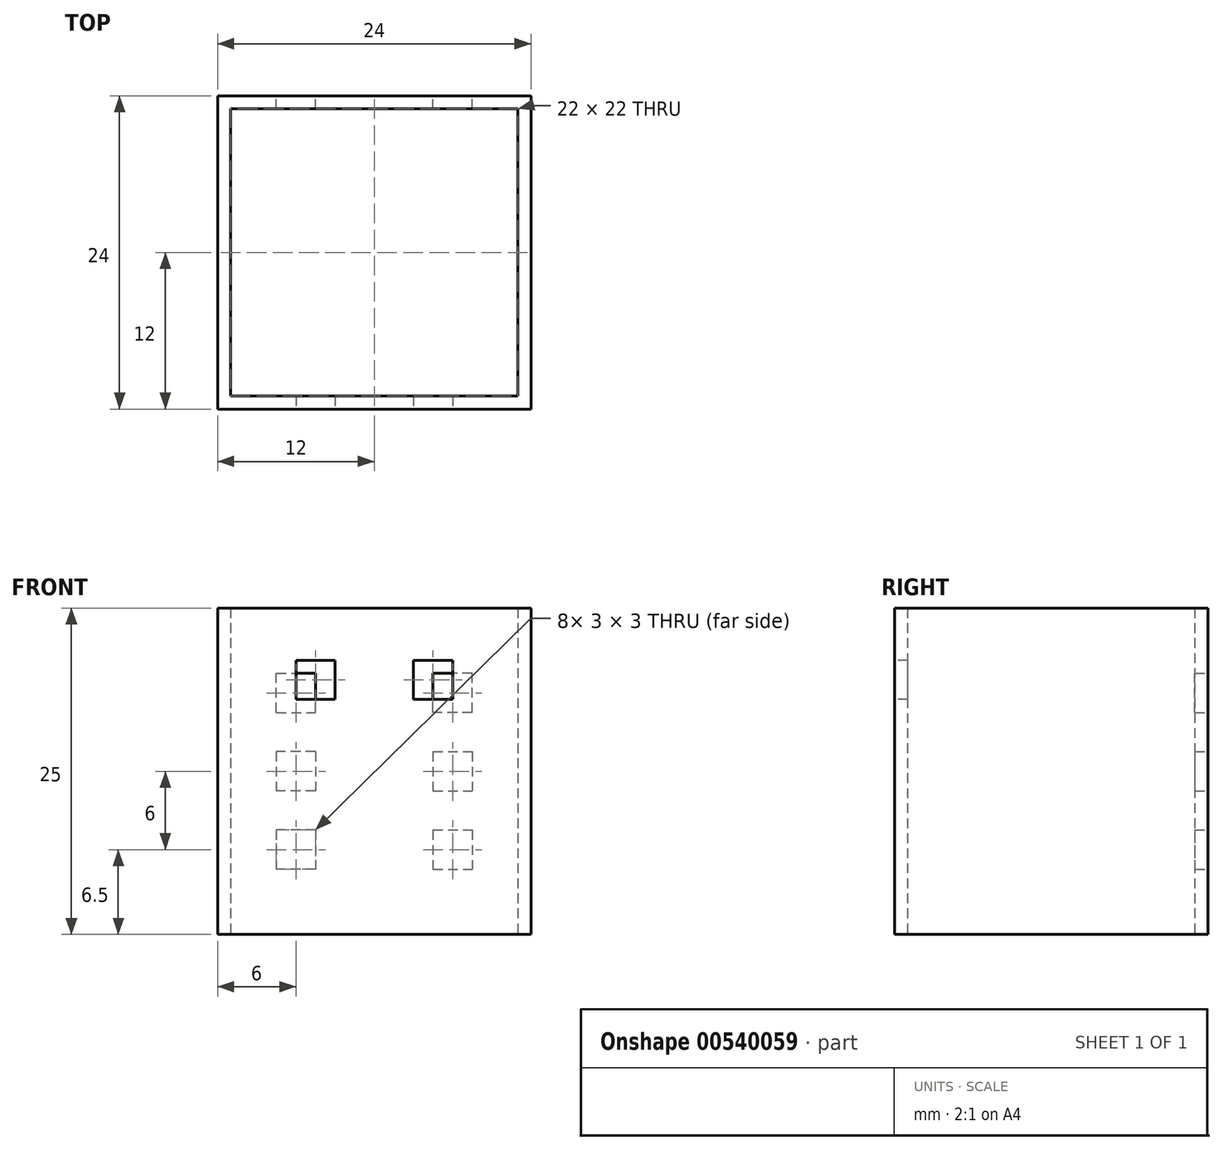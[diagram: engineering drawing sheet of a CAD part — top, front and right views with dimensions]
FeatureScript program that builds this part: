
annotation { "Feature Type Name" : "Feature", "Feature Type Description" : "" }
export const myFeature = defineFeature(function(context is Context, id is Id, definition is map)
    precondition{}
    {
        {
            var Q0;
            Q0=qCreatedBy(makeId("Top.planeOp"),FACE);
            var sketch = newSketch(context, id + "F0", { "sketchPlane" : qUnion([Q0])});
            skLineSegment(sketch, "E0.bottom", {"start": v(12, -12) * mm, "end": v(-12, -12) * mm});
            skLineSegment(sketch, "E0.top", {"start": v(12, 12) * mm, "end": v(-12, 12) * mm});
            skLineSegment(sketch, "E0.left", {"start": v(12, -12) * mm, "end": v(12, 12) * mm});
            skLineSegment(sketch, "E0.right", {"start": v(-12, -12) * mm, "end": v(-12, 12) * mm});
            skPoint(sketch, "E0.middle", {"position": v(0, 0) * mm});
            skLineSegment(sketch, "E1.bottom", {"start": v(11, -11) * mm, "end": v(-11, -11) * mm});
            skLineSegment(sketch, "E1.top", {"start": v(11, 11) * mm, "end": v(-11, 11) * mm});
            skLineSegment(sketch, "E1.left", {"start": v(11, -11) * mm, "end": v(11, 11) * mm});
            skLineSegment(sketch, "E1.right", {"start": v(-11, -11) * mm, "end": v(-11, 11) * mm});
            skSolve(sketch);
        }
        {
            var Q0;
            Q0=makeQuery(id+"F0.imprint","IMPRINT",FACE,{"disambiguationData":[TD([[makeQuery(id+"F0.imprint","IMPRINT",EDGE,{"derivedFrom":sQuery(id+"F0.wireOp",EDGE,"E0.bottom")}),-1.0]])]});
            extrude(context, id + "F1", {"entities" : qUnion([Q0]), "depth" : 25 * mm, "offsetDistance" : 25 * mm});
        }
        {
            var Q0;
            Q0=makeQuery(id+"F1.opExtrude","SWEPT_FACE",FACE,{"disambiguationData":[OSD([sQuery(id+"F0.wireOp",EDGE,"E0.bottom")])]});
            var sketch = newSketch(context, id + "F2", { "sketchPlane" : qUnion([Q0])});
            skLineSegment(sketch, "E2.0.0", {"start": v(-12, 0) * mm, "end": v(12, 0) * mm});
            skLineSegment(sketch, "E2.0.1", {"start": v(12, 0) * mm, "end": v(12, 25) * mm});
            skLineSegment(sketch, "E2.0.2", {"start": v(12, 25) * mm, "end": v(0, 25) * mm});
            skLineSegment(sketch, "E2.0.3", {"start": v(-12, 25) * mm, "end": v(-12, 0) * mm});
            skLineSegment(sketch, "E3", {"start": v(0, 25) * mm, "end": v(0, 0) * mm, "construction": true});
            skLineSegment(sketch, "E4.bottom", {"start": v(6, 18) * mm, "end": v(3, 18) * mm});
            skLineSegment(sketch, "E4.top", {"start": v(6, 21) * mm, "end": v(3, 21) * mm});
            skLineSegment(sketch, "E4.left", {"start": v(6, 18) * mm, "end": v(6, 21) * mm});
            skLineSegment(sketch, "E4.right", {"start": v(3, 18) * mm, "end": v(3, 21) * mm});
            skPoint(sketch, "E4.middle", {"position": v(4.5, 19.5) * mm});
            skPoint(sketch, "E4.middle.positionSnap0", {"position": v(6, 25) * mm});
            skPoint(sketch, "E4.centerSnap0", {"position": v(6, 25) * mm});
            skLineSegment(sketch, "E5.MirrorCS", {"start": v(-3, 18) * mm, "end": v(-3, 21) * mm});
            skLineSegment(sketch, "E6.MirrorCS", {"start": v(-6, 21) * mm, "end": v(-3, 21) * mm});
            skLineSegment(sketch, "E7.MirrorCS", {"start": v(-6, 18) * mm, "end": v(-6, 21) * mm});
            skLineSegment(sketch, "E8.MirrorCS", {"start": v(-6, 18) * mm, "end": v(-3, 18) * mm});
            skSolve(sketch);
        }
        {
            var Q0;
            Q0=makeQuery(id+"F2.imprint","IMPRINT",FACE,{"disambiguationData":[TD([[makeQuery(id+"F2.imprint","IMPRINT",EDGE,{"derivedFrom":sQuery(id+"F2.wireOp",EDGE,"E5.MirrorCS")}),1.0]])]});
            var Q1;
            Q1=makeQuery(id+"F2.imprint","IMPRINT",FACE,{"disambiguationData":[TD([[makeQuery(id+"F2.imprint","IMPRINT",EDGE,{"derivedFrom":sQuery(id+"F2.wireOp",EDGE,"E4.bottom")}),-1.0]])]});
            extrude(context, id + "F3", {"entities" : qUnion([Q0, Q1]), "operationType" : NewBodyOperationType.REMOVE, "endBound" : BoundingType.UP_TO_NEXT, "oppositeDirection" : true, "depth" : 25 * mm, "offsetDistance" : 25 * mm});
        }
        {
            var Q0;
            Q0=makeQuery(id+"F1.opExtrude","SWEPT_FACE",FACE,{"disambiguationData":[OSD([sQuery(id+"F0.wireOp",EDGE,"E0.top")])]});
            var sketch = newSketch(context, id + "F4", { "sketchPlane" : qUnion([Q0])});
            skLineSegment(sketch, "E9", {"start": v(0, 25) * mm, "end": v(0, 0) * mm, "construction": true});
            skLineSegment(sketch, "E10.bottom", {"start": v(7.5, 17) * mm, "end": v(4.5, 17) * mm});
            skLineSegment(sketch, "E10.top", {"start": v(7.5, 20) * mm, "end": v(4.5, 20) * mm});
            skLineSegment(sketch, "E10.left", {"start": v(7.5, 17) * mm, "end": v(7.5, 20) * mm});
            skLineSegment(sketch, "E10.right", {"start": v(4.5, 17) * mm, "end": v(4.5, 20) * mm});
            skPoint(sketch, "E10.middle", {"position": v(6, 18.5) * mm});
            skLineSegment(sketch, "E11.bottom", {"start": v(4.5, 14) * mm, "end": v(7.5, 14) * mm});
            skLineSegment(sketch, "E11.top", {"start": v(4.5, 11) * mm, "end": v(7.5, 11) * mm});
            skLineSegment(sketch, "E11.left", {"start": v(4.5, 14) * mm, "end": v(4.5, 11) * mm});
            skLineSegment(sketch, "E11.right", {"start": v(7.5, 14) * mm, "end": v(7.5, 11) * mm});
            skLineSegment(sketch, "E12.bottom", {"start": v(4.5, 8) * mm, "end": v(7.5, 8) * mm});
            skLineSegment(sketch, "E12.top", {"start": v(4.5, 5) * mm, "end": v(7.5, 5) * mm});
            skLineSegment(sketch, "E12.left", {"start": v(4.5, 8) * mm, "end": v(4.5, 5) * mm});
            skLineSegment(sketch, "E12.right", {"start": v(7.5, 8) * mm, "end": v(7.5, 5) * mm});
            skLineSegment(sketch, "E13", {"start": v(6, 5) * mm, "end": v(6, 0) * mm, "construction": true});
            skLineSegment(sketch, "E14", {"start": v(0, 25) * mm, "end": v(12, 25) * mm, "construction": true});
            skLineSegment(sketch, "E15", {"start": v(6, 25) * mm, "end": v(6, 20) * mm, "construction": true});
            skLineSegment(sketch, "E16", {"start": v(6, 17) * mm, "end": v(6, 14) * mm, "construction": true});
            skLineSegment(sketch, "E17", {"start": v(6, 11) * mm, "end": v(6, 8) * mm, "construction": true});
            skLineSegment(sketch, "E18.MirrorCS", {"start": v(-4.5, 17) * mm, "end": v(-4.5, 20) * mm});
            skLineSegment(sketch, "E19.MirrorCS", {"start": v(-7.5, 20) * mm, "end": v(-4.5, 20) * mm});
            skLineSegment(sketch, "E20.MirrorCS", {"start": v(-7.5, 17) * mm, "end": v(-7.5, 20) * mm});
            skLineSegment(sketch, "E21.MirrorCS", {"start": v(-7.5, 17) * mm, "end": v(-4.5, 17) * mm});
            skLineSegment(sketch, "E22.MirrorCS", {"start": v(-4.5, 14) * mm, "end": v(-7.5, 14) * mm});
            skLineSegment(sketch, "E23.MirrorCS", {"start": v(-7.5, 14) * mm, "end": v(-7.5, 11) * mm});
            skLineSegment(sketch, "E24.MirrorCS", {"start": v(-4.5, 11) * mm, "end": v(-7.5, 11) * mm});
            skLineSegment(sketch, "E25.MirrorCS", {"start": v(-4.5, 14) * mm, "end": v(-4.5, 11) * mm});
            skLineSegment(sketch, "E26.MirrorCS", {"start": v(-4.5, 8) * mm, "end": v(-7.5, 8) * mm});
            skLineSegment(sketch, "E27.MirrorCS", {"start": v(-7.5, 8) * mm, "end": v(-7.5, 5) * mm});
            skLineSegment(sketch, "E28.MirrorCS", {"start": v(-4.5, 5) * mm, "end": v(-7.5, 5) * mm});
            skLineSegment(sketch, "E29.MirrorCS", {"start": v(-4.5, 8) * mm, "end": v(-4.5, 5) * mm});
            skSolve(sketch);
        }
        {
            var Q0;
            Q0=makeQuery(id+"F4.imprint","IMPRINT",FACE,{"disambiguationData":[TD([[makeQuery(id+"F4.imprint","IMPRINT",EDGE,{"derivedFrom":sQuery(id+"F4.wireOp",EDGE,"E26.MirrorCS")}),1.0]])]});
            var Q1;
            Q1=makeQuery(id+"F4.imprint","IMPRINT",FACE,{"disambiguationData":[TD([[makeQuery(id+"F4.imprint","IMPRINT",EDGE,{"derivedFrom":sQuery(id+"F4.wireOp",EDGE,"E22.MirrorCS")}),1.0]])]});
            var Q2;
            Q2=makeQuery(id+"F4.imprint","IMPRINT",FACE,{"disambiguationData":[TD([[makeQuery(id+"F4.imprint","IMPRINT",EDGE,{"derivedFrom":sQuery(id+"F4.wireOp",EDGE,"E18.MirrorCS")}),1.0]])]});
            var Q3;
            Q3=makeQuery(id+"F4.imprint","IMPRINT",FACE,{"disambiguationData":[TD([[makeQuery(id+"F4.imprint","IMPRINT",EDGE,{"derivedFrom":sQuery(id+"F4.wireOp",EDGE,"E10.bottom")}),-1.0]])]});
            var Q4;
            Q4=makeQuery(id+"F4.imprint","IMPRINT",FACE,{"disambiguationData":[TD([[makeQuery(id+"F4.imprint","IMPRINT",EDGE,{"derivedFrom":sQuery(id+"F4.wireOp",EDGE,"E11.bottom")}),-1.0]])]});
            var Q5;
            Q5=makeQuery(id+"F4.imprint","IMPRINT",FACE,{"disambiguationData":[TD([[makeQuery(id+"F4.imprint","IMPRINT",EDGE,{"derivedFrom":sQuery(id+"F4.wireOp",EDGE,"E12.bottom")}),-1.0]])]});
            extrude(context, id + "F5", {"entities" : qUnion([Q0, Q1, Q2, Q3, Q4, Q5]), "operationType" : NewBodyOperationType.REMOVE, "endBound" : BoundingType.UP_TO_NEXT, "oppositeDirection" : true, "depth" : 25 * mm, "offsetDistance" : 25 * mm});
        }
    });
